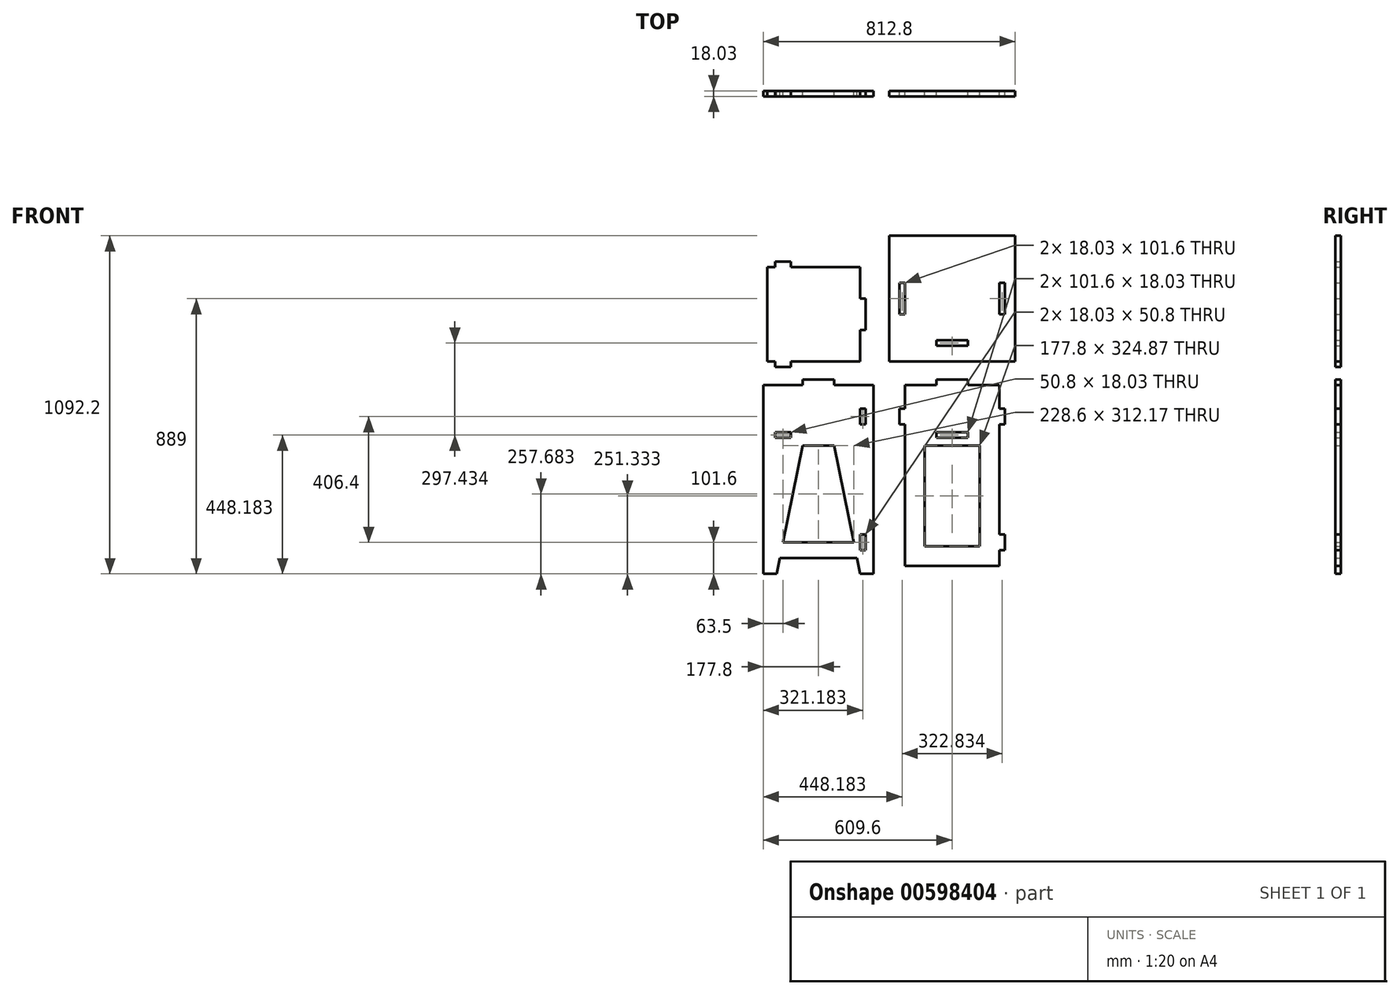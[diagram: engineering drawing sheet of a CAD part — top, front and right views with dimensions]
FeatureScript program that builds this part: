
annotation { "Feature Type Name" : "Feature", "Feature Type Description" : "" }
export const myFeature = defineFeature(function(context is Context, id is Id, definition is map)
    precondition{}
    {
        {
            var Q0;
            Q0=qCreatedBy(makeId("Front.planeOp"),FACE);
            var sketch = newSketch(context, id + "F0", { "sketchPlane" : qUnion([Q0])});
            skLineSegment(sketch, "E0.bottom", {"start": v(-177.8, 304.8) * mm, "end": v(177.8, 304.8) * mm});
            skLineSegment(sketch, "E0.top", {"start": v(-177.8, -304.8) * mm, "end": v(177.8, -304.8) * mm});
            skLineSegment(sketch, "E0.left", {"start": v(-177.8, 304.8) * mm, "end": v(-177.8, -304.8) * mm});
            skLineSegment(sketch, "E0.right", {"start": v(177.8, 304.8) * mm, "end": v(177.8, -304.8) * mm});
            skPoint(sketch, "E0.middle", {"position": v(0, 0) * mm});
            skLineSegment(sketch, "E1.bottom", {"start": v(-114.3, -304.8) * mm, "end": v(114.3, -304.8) * mm});
            skLineSegment(sketch, "E1.top", {"start": v(-114.3, -254) * mm, "end": v(114.3, -254) * mm});
            skLineSegment(sketch, "E1.left", {"start": v(-114.3, -304.8) * mm, "end": v(-114.3, -254) * mm});
            skLineSegment(sketch, "E1.right", {"start": v(114.3, -304.8) * mm, "end": v(114.3, -254) * mm});
            skPoint(sketch, "E1.middle", {"position": v(0, -279.4) * mm});
            skPoint(sketch, "E1.middle.positionSnap0", {"position": v(0, -304.8) * mm});
            skPoint(sketch, "E1.centerSnap0", {"position": v(0, -304.8) * mm});
            skLineSegment(sketch, "E2.bottom", {"start": v(-88.9, 134.37) * mm, "end": v(-139.7, 134.37) * mm});
            skLineSegment(sketch, "E2.top", {"start": v(-88.9, 152.4) * mm, "end": v(-139.7, 152.4) * mm});
            skLineSegment(sketch, "E2.left", {"start": v(-88.9, 134.37) * mm, "end": v(-88.9, 152.4) * mm});
            skLineSegment(sketch, "E2.right", {"start": v(-139.7, 134.37) * mm, "end": v(-139.7, 152.4) * mm});
            skPoint(sketch, "E2.middle", {"position": v(-114.3, 143.38) * mm});
            skLineSegment(sketch, "E3.bottom", {"start": v(152.4, 228.6) * mm, "end": v(134.37, 228.6) * mm});
            skLineSegment(sketch, "E3.top", {"start": v(152.4, 177.8) * mm, "end": v(134.37, 177.8) * mm});
            skLineSegment(sketch, "E3.left", {"start": v(152.4, 228.6) * mm, "end": v(152.4, 177.8) * mm});
            skLineSegment(sketch, "E3.right", {"start": v(134.37, 228.6) * mm, "end": v(134.37, 177.8) * mm});
            skPoint(sketch, "E3.middle", {"position": v(143.38, 203.2) * mm});
            skLineSegment(sketch, "E4", {"start": v(0, 0) * mm, "end": v(177.8, 0) * mm, "construction": true});
            skLineSegment(sketch, "E5.MirrorCS", {"start": v(134.37, -228.6) * mm, "end": v(134.37, -177.8) * mm});
            skLineSegment(sketch, "E6.MirrorCS", {"start": v(152.4, -228.6) * mm, "end": v(134.37, -228.6) * mm});
            skPoint(sketch, "E7.MirrorP", {"position": v(143.38, -203.2) * mm});
            skLineSegment(sketch, "E8.MirrorCS", {"start": v(152.4, -177.8) * mm, "end": v(134.37, -177.8) * mm});
            skLineSegment(sketch, "E9.MirrorCS", {"start": v(152.4, -228.6) * mm, "end": v(152.4, -177.8) * mm});
            skLineSegment(sketch, "E10.bottom", {"start": v(279.4, 304.8) * mm, "end": v(584.2, 304.8) * mm});
            skLineSegment(sketch, "E10.top", {"start": v(279.4, -304.8) * mm, "end": v(584.2, -304.8) * mm});
            skLineSegment(sketch, "E10.left", {"start": v(279.4, 304.8) * mm, "end": v(279.4, -304.8) * mm});
            skLineSegment(sketch, "E10.right", {"start": v(584.2, 304.8) * mm, "end": v(584.2, -304.8) * mm});
            skPoint(sketch, "E10.middle", {"position": v(431.8, 0) * mm});
            skLineSegment(sketch, "E11.bottom", {"start": v(279.4, 228.6) * mm, "end": v(261.37, 228.6) * mm});
            skLineSegment(sketch, "E11.top", {"start": v(279.4, 177.8) * mm, "end": v(261.37, 177.8) * mm});
            skLineSegment(sketch, "E11.left", {"start": v(279.4, 228.6) * mm, "end": v(279.4, 177.8) * mm});
            skLineSegment(sketch, "E11.right", {"start": v(261.37, 228.6) * mm, "end": v(261.37, 177.8) * mm});
            skPoint(sketch, "E11.middle", {"position": v(270.38, 203.2) * mm});
            skLineSegment(sketch, "E12.bottom", {"start": v(261.37, -177.8) * mm, "end": v(279.4, -177.8) * mm});
            skLineSegment(sketch, "E12.top", {"start": v(261.37, -228.6) * mm, "end": v(279.4, -228.6) * mm});
            skLineSegment(sketch, "E12.left", {"start": v(261.37, -177.8) * mm, "end": v(261.37, -228.6) * mm});
            skLineSegment(sketch, "E12.right", {"start": v(279.4, -177.8) * mm, "end": v(279.4, -228.6) * mm});
            skPoint(sketch, "E12.middle", {"position": v(270.38, -203.2) * mm});
            skPoint(sketch, "E12.middle.positionSnap0", {"position": v(270.38, 177.8) * mm});
            skPoint(sketch, "E12.centerSnap0", {"position": v(270.38, 177.8) * mm});
            skLineSegment(sketch, "E13", {"start": v(431.8, 0) * mm, "end": v(431.8, 304.8) * mm, "construction": true});
            skLineSegment(sketch, "E14.MirrorCS", {"start": v(584.2, 177.8) * mm, "end": v(602.23, 177.8) * mm});
            skLineSegment(sketch, "E15.MirrorCS", {"start": v(602.23, -228.6) * mm, "end": v(584.2, -228.6) * mm});
            skLineSegment(sketch, "E16.MirrorCS", {"start": v(584.2, 228.6) * mm, "end": v(602.23, 228.6) * mm});
            skLineSegment(sketch, "E17.MirrorCS", {"start": v(602.23, -177.8) * mm, "end": v(584.2, -177.8) * mm});
            skLineSegment(sketch, "E18.MirrorCS", {"start": v(602.23, 228.6) * mm, "end": v(602.23, 177.8) * mm});
            skLineSegment(sketch, "E19.MirrorCS", {"start": v(602.23, -177.8) * mm, "end": v(602.23, -228.6) * mm});
            skPoint(sketch, "E20.MirrorP", {"position": v(593.22, 177.8) * mm});
            skLineSegment(sketch, "E21.MirrorCS", {"start": v(584.2, -177.8) * mm, "end": v(584.2, -228.6) * mm});
            skLineSegment(sketch, "E22.MirrorCS", {"start": v(584.2, 228.6) * mm, "end": v(584.2, 177.8) * mm});
            skPoint(sketch, "E23.MirrorP", {"position": v(593.22, -203.2) * mm});
            skPoint(sketch, "E24.MirrorP", {"position": v(593.22, 203.2) * mm});
            skLineSegment(sketch, "E25", {"start": v(279.4, -279.4) * mm, "end": v(584.2, -279.4) * mm});
            skLineSegment(sketch, "E26.bottom", {"start": v(381, 152.4) * mm, "end": v(482.6, 152.4) * mm});
            skLineSegment(sketch, "E26.top", {"start": v(381, 134.37) * mm, "end": v(482.6, 134.37) * mm});
            skLineSegment(sketch, "E26.left", {"start": v(381, 152.4) * mm, "end": v(381, 134.37) * mm});
            skLineSegment(sketch, "E26.right", {"start": v(482.6, 152.4) * mm, "end": v(482.6, 134.37) * mm});
            skPoint(sketch, "E26.middle", {"position": v(431.8, 143.38) * mm});
            skLineSegment(sketch, "E27.bottom", {"start": v(342.9, 108.97) * mm, "end": v(520.7, 108.97) * mm});
            skLineSegment(sketch, "E27.top", {"start": v(342.9, -215.9) * mm, "end": v(520.7, -215.9) * mm});
            skLineSegment(sketch, "E27.left", {"start": v(342.9, 108.97) * mm, "end": v(342.9, -215.9) * mm});
            skLineSegment(sketch, "E27.right", {"start": v(520.7, 108.97) * mm, "end": v(520.7, -215.9) * mm});
            skPoint(sketch, "E27.middle", {"position": v(431.8, -53.47) * mm});
            skLineSegment(sketch, "E28.bottom", {"start": v(134.37, 381) * mm, "end": v(-165.1, 381) * mm});
            skLineSegment(sketch, "E28.top", {"start": v(134.37, 685.8) * mm, "end": v(-165.1, 685.8) * mm});
            skLineSegment(sketch, "E28.left", {"start": v(134.37, 381) * mm, "end": v(134.37, 685.8) * mm});
            skLineSegment(sketch, "E28.right", {"start": v(-165.1, 381) * mm, "end": v(-165.1, 685.8) * mm});
            skLineSegment(sketch, "E29.bottom", {"start": v(-88.9, 381) * mm, "end": v(-139.7, 381) * mm});
            skLineSegment(sketch, "E29.top", {"start": v(-88.9, 362.97) * mm, "end": v(-139.7, 362.97) * mm});
            skLineSegment(sketch, "E29.left", {"start": v(-88.9, 381) * mm, "end": v(-88.9, 362.97) * mm});
            skLineSegment(sketch, "E29.right", {"start": v(-139.7, 381) * mm, "end": v(-139.7, 362.97) * mm});
            skLineSegment(sketch, "E30.bottom", {"start": v(134.37, 584.2) * mm, "end": v(152.4, 584.2) * mm});
            skLineSegment(sketch, "E30.top", {"start": v(134.37, 482.6) * mm, "end": v(152.4, 482.6) * mm});
            skLineSegment(sketch, "E30.left", {"start": v(134.37, 584.2) * mm, "end": v(134.37, 482.6) * mm});
            skLineSegment(sketch, "E30.right", {"start": v(152.4, 584.2) * mm, "end": v(152.4, 482.6) * mm});
            skPoint(sketch, "E30.middle", {"position": v(143.38, 533.4) * mm});
            skPoint(sketch, "E30.middle.positionSnap0", {"position": v(134.37, 533.4) * mm});
            skPoint(sketch, "E30.centerSnap0", {"position": v(134.37, 533.4) * mm});
            skLineSegment(sketch, "E31", {"start": v(-165.1, 533.4) * mm, "end": v(0, 533.4) * mm, "construction": true});
            skLineSegment(sketch, "E32.MirrorCS", {"start": v(-139.7, 685.8) * mm, "end": v(-139.7, 703.83) * mm});
            skLineSegment(sketch, "E33.MirrorCS", {"start": v(-88.9, 685.8) * mm, "end": v(-88.9, 703.83) * mm});
            skLineSegment(sketch, "E34.MirrorCS", {"start": v(-88.9, 703.83) * mm, "end": v(-139.7, 703.83) * mm});
            skLineSegment(sketch, "E35.MirrorCS", {"start": v(-88.9, 685.8) * mm, "end": v(-139.7, 685.8) * mm});
            skLineSegment(sketch, "E36.bottom", {"start": v(-50.8, 304.8) * mm, "end": v(50.8, 304.8) * mm});
            skLineSegment(sketch, "E36.top", {"start": v(-50.8, 322.83) * mm, "end": v(50.8, 322.83) * mm});
            skLineSegment(sketch, "E36.left", {"start": v(-50.8, 304.8) * mm, "end": v(-50.8, 322.83) * mm});
            skLineSegment(sketch, "E36.right", {"start": v(50.8, 304.8) * mm, "end": v(50.8, 322.83) * mm});
            skPoint(sketch, "E36.middle", {"position": v(0, 313.82) * mm});
            skPoint(sketch, "E36.middle.positionSnap0", {"position": v(0, 304.8) * mm});
            skPoint(sketch, "E36.centerSnap0", {"position": v(0, 304.8) * mm});
            skLineSegment(sketch, "E37.bottom", {"start": v(381, 304.8) * mm, "end": v(482.6, 304.8) * mm});
            skLineSegment(sketch, "E37.top", {"start": v(381, 322.83) * mm, "end": v(482.6, 322.83) * mm});
            skLineSegment(sketch, "E37.left", {"start": v(381, 304.8) * mm, "end": v(381, 322.83) * mm});
            skLineSegment(sketch, "E37.right", {"start": v(482.6, 304.8) * mm, "end": v(482.6, 322.83) * mm});
            skPoint(sketch, "E37.middle", {"position": v(431.8, 313.82) * mm});
            skPoint(sketch, "E37.middle.positionSnap0", {"position": v(50.8, 313.82) * mm});
            skPoint(sketch, "E37.centerSnap0", {"position": v(50.8, 313.82) * mm});
            skLineSegment(sketch, "E38.bottom", {"start": v(228.6, 381) * mm, "end": v(635, 381) * mm});
            skLineSegment(sketch, "E38.top", {"start": v(228.6, 787.4) * mm, "end": v(635, 787.4) * mm});
            skLineSegment(sketch, "E38.left", {"start": v(228.6, 381) * mm, "end": v(228.6, 787.4) * mm});
            skLineSegment(sketch, "E38.right", {"start": v(635, 381) * mm, "end": v(635, 787.4) * mm});
            skPoint(sketch, "E38.middle", {"position": v(431.8, 584.2) * mm});
            skLineSegment(sketch, "E39.bottom", {"start": v(381, 431.8) * mm, "end": v(482.6, 431.8) * mm});
            skLineSegment(sketch, "E39.top", {"start": v(381, 449.83) * mm, "end": v(482.6, 449.83) * mm});
            skLineSegment(sketch, "E39.left", {"start": v(381, 431.8) * mm, "end": v(381, 449.83) * mm});
            skLineSegment(sketch, "E39.right", {"start": v(482.6, 431.8) * mm, "end": v(482.6, 449.83) * mm});
            skPoint(sketch, "E39.middle", {"position": v(431.8, 440.82) * mm});
            skPoint(sketch, "E39.middle.positionSnap0", {"position": v(431.8, 381) * mm});
            skPoint(sketch, "E39.centerSnap0", {"position": v(431.8, 381) * mm});
            skLineSegment(sketch, "E40.bottom", {"start": v(261.37, 635) * mm, "end": v(279.4, 635) * mm});
            skLineSegment(sketch, "E40.top", {"start": v(261.37, 533.4) * mm, "end": v(279.4, 533.4) * mm});
            skLineSegment(sketch, "E40.left", {"start": v(261.37, 635) * mm, "end": v(261.37, 533.4) * mm});
            skLineSegment(sketch, "E40.right", {"start": v(279.4, 635) * mm, "end": v(279.4, 533.4) * mm});
            skPoint(sketch, "E40.middle", {"position": v(270.38, 584.2) * mm});
            skPoint(sketch, "E40.middle.positionSnap0", {"position": v(228.6, 584.2) * mm});
            skPoint(sketch, "E40.centerSnap0", {"position": v(228.6, 584.2) * mm});
            skLineSegment(sketch, "E41.MirrorCS", {"start": v(602.23, 635) * mm, "end": v(584.2, 635) * mm});
            skLineSegment(sketch, "E42.MirrorCS", {"start": v(602.23, 533.4) * mm, "end": v(584.2, 533.4) * mm});
            skLineSegment(sketch, "E43.MirrorCS", {"start": v(602.23, 635) * mm, "end": v(602.23, 533.4) * mm});
            skPoint(sketch, "E44.MirrorP", {"position": v(593.22, 584.2) * mm});
            skLineSegment(sketch, "E45.MirrorCS", {"start": v(584.2, 635) * mm, "end": v(584.2, 533.4) * mm});
            skLineSegment(sketch, "E46", {"start": v(-50.8, 108.97) * mm, "end": v(50.8, 108.97) * mm});
            skLineSegment(sketch, "E47", {"start": v(50.8, 108.97) * mm, "end": v(114.3, -203.2) * mm});
            skLineSegment(sketch, "E48", {"start": v(114.3, -203.2) * mm, "end": v(-114.3, -203.2) * mm});
            skLineSegment(sketch, "E49", {"start": v(-114.3, -203.2) * mm, "end": v(-50.8, 108.97) * mm});
            skLineSegment(sketch, "E50", {"start": v(-114.3, -203.2) * mm, "end": v(-134.97, -304.8) * mm, "construction": true});
            skLineSegment(sketch, "E51", {"start": v(-114.3, -254) * mm, "end": v(-124.63, -254) * mm});
            skLineSegment(sketch, "E52", {"start": v(-124.63, -254) * mm, "end": v(-134.97, -304.8) * mm});
            skLineSegment(sketch, "E53", {"start": v(0, 0) * mm, "end": v(0, 108.97) * mm, "construction": true});
            skLineSegment(sketch, "E54.MirrorCS", {"start": v(124.63, -254) * mm, "end": v(134.97, -304.8) * mm});
            skLineSegment(sketch, "E55.MirrorCS", {"start": v(114.3, -254) * mm, "end": v(124.63, -254) * mm});
            skSolve(sketch);
        }
        {
            var Q0;
            {var subQ4=sQuery(id+"F0.wireOp",EDGE,"E28.right");Q0=makeQuery(id+"F0.imprint","IMPRINT",FACE,{"disambiguationData":[TD([[makeQuery(id+"F0.imprint","IMPRINT",EDGE,{"derivedFrom":subQ4}),-1.0]])]});}
            var Q1;
            {var subQ0=sQuery(id+"F0.wireOp",EDGE,"E32.MirrorCS");Q1=makeQuery(id+"F0.imprint","IMPRINT",FACE,{"disambiguationData":[TD([[makeQuery(id+"F0.imprint","IMPRINT",EDGE,{"derivedFrom":subQ0}),-1.0]])]});}
            var Q2;
            Q2=makeQuery(id+"F0.imprint","IMPRINT",FACE,{"disambiguationData":[TD([[makeQuery(id+"F0.imprint","IMPRINT",EDGE,{"derivedFrom":sQuery(id+"F0.wireOp",EDGE,"E29.top")}),-1.0]])]});
            var Q3;
            {var subQ0=sQuery(id+"F0.wireOp",EDGE,"E30.bottom");Q3=makeQuery(id+"F0.imprint","IMPRINT",FACE,{"disambiguationData":[TD([[makeQuery(id+"F0.imprint","IMPRINT",EDGE,{"derivedFrom":subQ0}),-1.0]])]});}
            var Q4;
            Q4=makeQuery(id+"F0.imprint","IMPRINT",FACE,{"disambiguationData":[TD([[makeQuery(id+"F0.imprint","IMPRINT",EDGE,{"derivedFrom":sQuery(id+"F0.wireOp",EDGE,"E38.bottom")}),1.0]])]});
            var Q5;
            {var subQ8=sQuery(id+"F0.wireOp",EDGE,"E25");Q5=makeQuery(id+"F0.imprint","IMPRINT",FACE,{"disambiguationData":[TD([[makeQuery(id+"F0.imprint","IMPRINT",EDGE,{"derivedFrom":subQ8}),1.0]])]});}
            var Q6;
            {var subQ2=sQuery(id+"F0.wireOp",EDGE,"E11.bottom");Q6=makeQuery(id+"F0.imprint","IMPRINT",FACE,{"disambiguationData":[TD([[makeQuery(id+"F0.imprint","IMPRINT",EDGE,{"derivedFrom":subQ2}),1.0]])]});}
            var Q7;
            Q7=makeQuery(id+"F0.imprint","IMPRINT",FACE,{"disambiguationData":[TD([[makeQuery(id+"F0.imprint","IMPRINT",EDGE,{"derivedFrom":sQuery(id+"F0.wireOp",EDGE,"E37.top")}),-1.0]])]});
            var Q8;
            {var subQ0=sQuery(id+"F0.wireOp",EDGE,"E14.MirrorCS");Q8=makeQuery(id+"F0.imprint","IMPRINT",FACE,{"disambiguationData":[TD([[makeQuery(id+"F0.imprint","IMPRINT",EDGE,{"derivedFrom":subQ0}),1.0]])]});}
            var Q9;
            {var subQ0=sQuery(id+"F0.wireOp",EDGE,"E15.MirrorCS");Q9=makeQuery(id+"F0.imprint","IMPRINT",FACE,{"disambiguationData":[TD([[makeQuery(id+"F0.imprint","IMPRINT",EDGE,{"derivedFrom":subQ0}),-1.0]])]});}
            var Q10;
            {var subQ6=sQuery(id+"F0.wireOp",EDGE,"E0.left");Q10=makeQuery(id+"F0.imprint","IMPRINT",FACE,{"disambiguationData":[TD([[makeQuery(id+"F0.imprint","IMPRINT",EDGE,{"derivedFrom":subQ6}),1.0]])]});}
            var Q11;
            Q11=makeQuery(id+"F0.imprint","IMPRINT",FACE,{"disambiguationData":[TD([[makeQuery(id+"F0.imprint","IMPRINT",EDGE,{"derivedFrom":sQuery(id+"F0.wireOp",EDGE,"E36.top")}),-1.0]])]});
            extrude(context, id + "F1", {"entities" : qUnion([Q0, Q1, Q2, Q3, Q4, Q5, Q6, Q7, Q8, Q9, Q10, Q11]), "depth" : 18.03 * mm, "offsetDistance" : 25.4 * mm});
        }
    });
